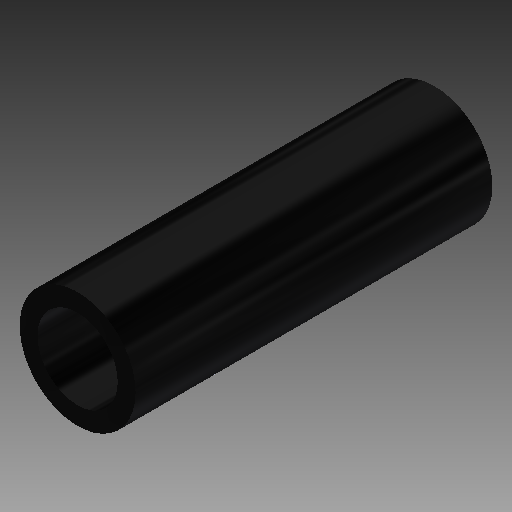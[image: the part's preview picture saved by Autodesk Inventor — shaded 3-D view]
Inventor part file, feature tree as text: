
AUTODESK INVENTOR PART (.ipt)
format: ipt  version: 2019 (Build 230136000, 136)  size: 105,984 bytes
history: native  units: mm
features: extrude x1, sketch x1
ambient origin geometry x8: Origin, YZ Plane, XZ Plane, XY Plane, X Axis, Y Axis, Z Axis, Center Point
bodies: Solid1 (feature_tree)
feature tree (2):
  extrude  "Extrusion1"  Depth=20.0mm
  sketch  "Sketch1"  dims[d0=4.5mm d1=6.5mm d2=20.0mm d3=0.0mm]
